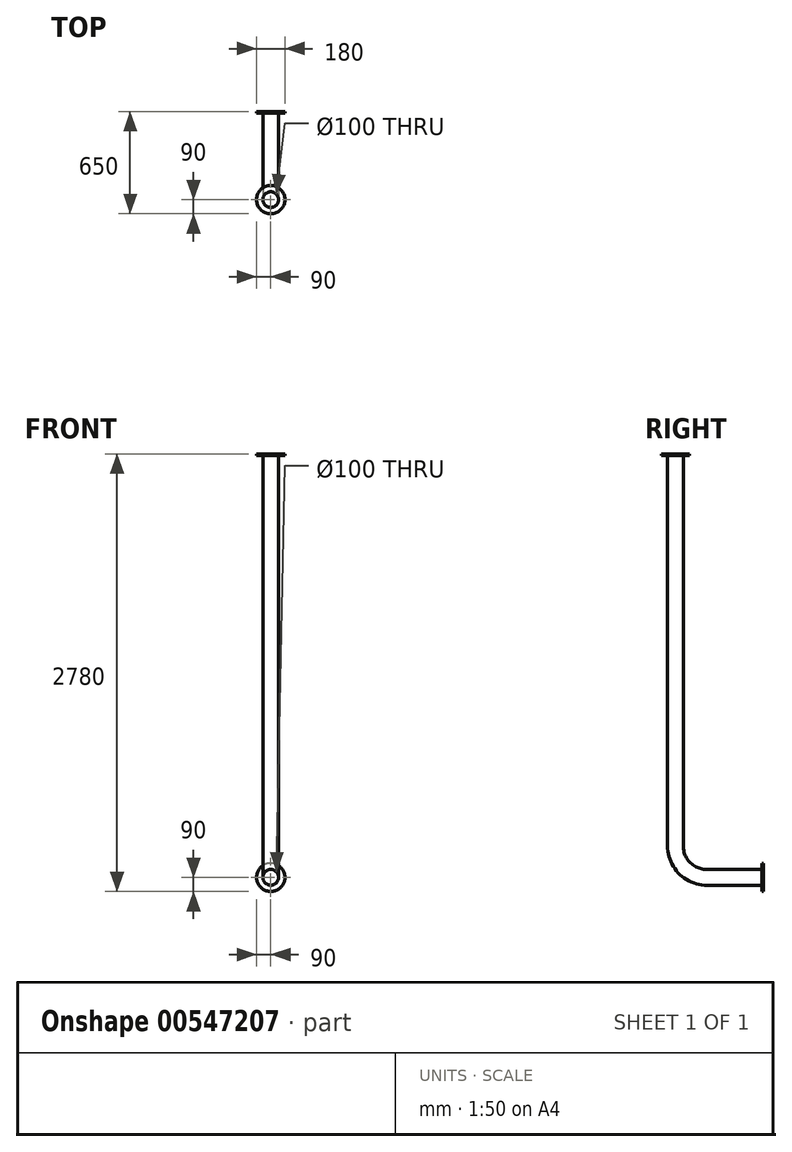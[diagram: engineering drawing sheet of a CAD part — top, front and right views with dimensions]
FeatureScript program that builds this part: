
annotation { "Feature Type Name" : "Feature", "Feature Type Description" : "" }
export const myFeature = defineFeature(function(context is Context, id is Id, definition is map)
    precondition{}
    {
        {
            var Q0;
            Q0=qCreatedBy(makeId("Front.planeOp"),FACE);
            var sketch = newSketch(context, id + "F0", { "sketchPlane" : qUnion([Q0])});
            skCircle(sketch, "E0", {"center": v(0, 0) * mm, "radius": 50 * mm});
            skSolve(sketch);
        }
        {
            var Q0;
            Q0=qCreatedBy(makeId("Right.planeOp"),FACE);
            var sketch = newSketch(context, id + "F1", { "sketchPlane" : qUnion([Q0])});
            skLineSegment(sketch, "E1", {"start": v(0, 0) * mm, "end": v(-350, 0) * mm});
            skLineSegment(sketch, "E2", {"start": v(-550, 200) * mm, "end": v(-550, 2680) * mm});
            skPoint(sketch, "E3.visualSharp", {"position": v(-550, 0) * mm});
            skArc(sketch, "E3.filletArc", {"start": v(-550, 200) * mm, "mid": v(-491.42, 58.58) * mm, "end": v(-350, 0) * mm});
            skSolve(sketch);
        }
        {
            var Q0;
            Q0=makeQuery(id+"F0.imprint","IMPRINT",FACE,{"disambiguationData":[TD([[makeQuery(id+"F0.imprint","IMPRINT",EDGE,{"derivedFrom":sQuery(id+"F0.wireOp",EDGE,"E0")}),1.0]])]});
            var Q1;
            Q1=sQuery(id+"F1.wireOp",EDGE,"E1");
            var Q2;
            Q2=sQuery(id+"F1.wireOp",EDGE,"E2");
            var Q3;
            Q3=sQuery(id+"F1.wireOp",EDGE,"E3.filletArc");
            sweep(context, id + "F2", {"profiles" : qUnion([Q0]), "path" : qUnion([Q1, Q2, Q3])});
        }
        {
            var Q0;
            Q0=makeQuery(id+"F2.opSweep","CAP_FACE",FACE,{"disambiguationData":[OSD([sQuery(id+"F0.wireOp",EDGE,"E0"),sQuery(id+"F1.wireOp",VERTEX,"E1.start")])],"isStart":true});
            var sketch = newSketch(context, id + "F3", { "sketchPlane" : qUnion([Q0])});
            skCircle(sketch, "E4", {"center": v(0, 0) * mm, "radius": 90 * mm});
            skSolve(sketch);
        }
        {
            var Q0;
            Q0=makeQuery(id+"F3.imprint","IMPRINT",FACE,{"disambiguationData":[TD([[makeQuery(id+"F3.imprint","IMPRINT",EDGE,{"derivedFrom":sQuery(id+"F3.wireOp",EDGE,"E4")}),1.0]])]});
            extrude(context, id + "F4", {"entities" : qUnion([Q0]), "depth" : 10 * mm, "offsetDistance" : 25 * mm});
        }
        {
            var Q0;
            Q0=makeQuery(id+"F2.opSweep","CAP_FACE",FACE,{"disambiguationData":[OSD([sQuery(id+"F0.wireOp",EDGE,"E0"),sQuery(id+"F1.wireOp",VERTEX,"E2.end")])],"isStart":false});
            var sketch = newSketch(context, id + "F5", { "sketchPlane" : qUnion([Q0])});
            skCircle(sketch, "E5", {"center": v(0, -550) * mm, "radius": 90 * mm});
            skSolve(sketch);
        }
        {
            var Q0;
            Q0=makeQuery(id+"F5.imprint","IMPRINT",FACE,{"disambiguationData":[TD([[makeQuery(id+"F5.imprint","IMPRINT",EDGE,{"derivedFrom":sQuery(id+"F5.wireOp",EDGE,"E5")}),1.0]])]});
            extrude(context, id + "F6", {"entities" : qUnion([Q0]), "depth" : 10 * mm, "offsetDistance" : 25 * mm});
        }
    });
